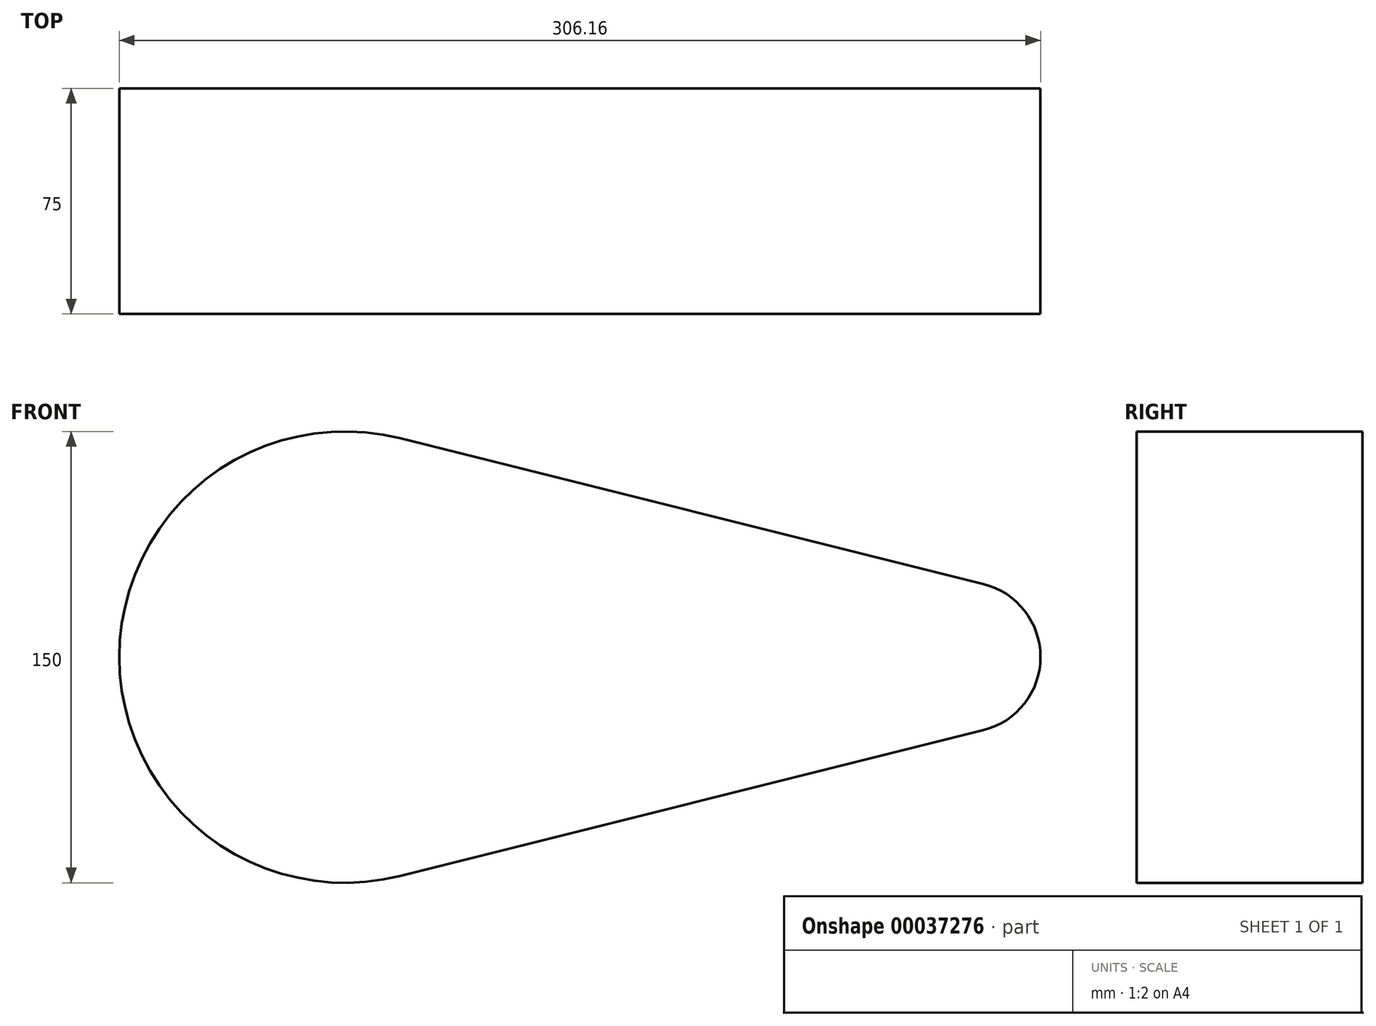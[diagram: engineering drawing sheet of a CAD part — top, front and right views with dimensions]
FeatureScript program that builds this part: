
annotation { "Feature Type Name" : "Feature", "Feature Type Description" : "" }
export const myFeature = defineFeature(function(context is Context, id is Id, definition is map)
    precondition{}
    {
        {
            var Q0;
            Q0=qCreatedBy(makeId("Front.planeOp"),FACE);
            var sketch = newSketch(context, id + "F0", { "sketchPlane" : qUnion([Q0])});
            skCircle(sketch, "E0", {"center": v(0, 0) * mm, "radius": 75 * mm});
            skCircle(sketch, "E1", {"center": v(206.16, 0) * mm, "radius": 25 * mm});
            skLineSegment(sketch, "E2", {"start": v(18.2, 72.76) * mm, "end": v(212.22, 24.25) * mm});
            skLineSegment(sketch, "E3", {"start": v(18.2, -72.76) * mm, "end": v(212.22, -24.25) * mm});
            skSolve(sketch);
        }
        {
            var Q0;
            {var subQ0=sQuery(id+"F0.wireOp",EDGE,"E0");var subQ2=makeQuery(id+"F0.imprint","INTERSECT",VERTEX,{"derivedFrom":[subQ0,sQuery(id+"F0.wireOp",EDGE,"E2")]});Q0=makeQuery(id+"F0.imprint","IMPRINT",FACE,{"disambiguationData":[TD([[makeQuery(id+"F0.imprint","IMPRINT",EDGE,{"disambiguationData":[TD([[subQ2,-1.0]])],"derivedFrom":subQ0}),1.0]])]});}
            var Q1;
            {var subQ1=sQuery(id+"F0.wireOp",EDGE,"E2");Q1=makeQuery(id+"F0.imprint","IMPRINT",FACE,{"disambiguationData":[TD([[makeQuery(id+"F0.imprint","IMPRINT",EDGE,{"derivedFrom":subQ1}),-1.0]])]});}
            var Q2;
            {var subQ0=sQuery(id+"F0.wireOp",EDGE,"E1");var subQ2=makeQuery(id+"F0.imprint","INTERSECT",VERTEX,{"derivedFrom":[subQ0,sQuery(id+"F0.wireOp",EDGE,"E2")]});Q2=makeQuery(id+"F0.imprint","IMPRINT",FACE,{"disambiguationData":[TD([[makeQuery(id+"F0.imprint","IMPRINT",EDGE,{"disambiguationData":[TD([[subQ2,-1.0]])],"derivedFrom":subQ0}),1.0]])]});}
            extrude(context, id + "F1", {"entities" : qUnion([Q0, Q1, Q2]), "depth" : 75 * mm});
        }
    });
